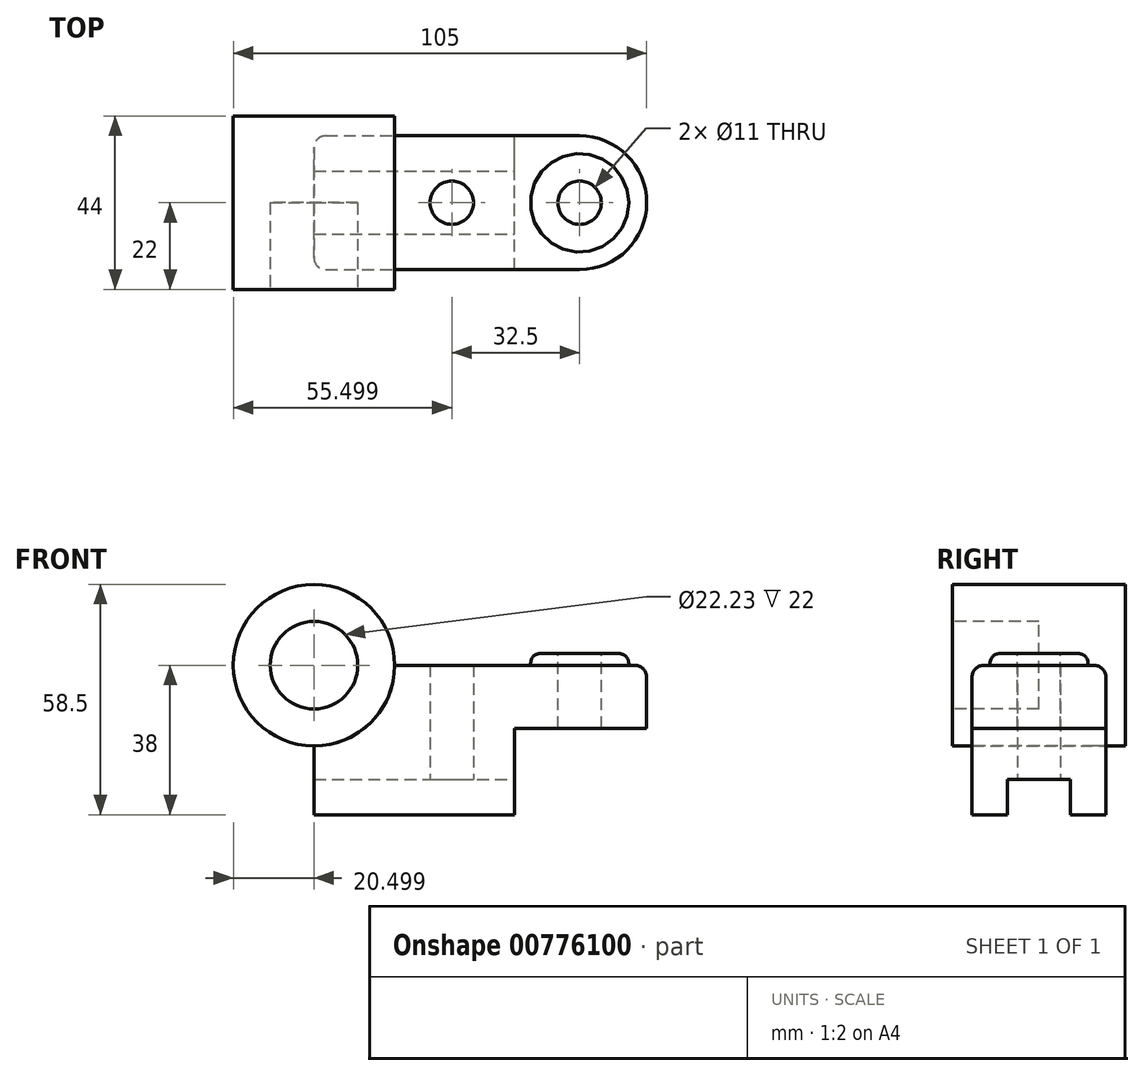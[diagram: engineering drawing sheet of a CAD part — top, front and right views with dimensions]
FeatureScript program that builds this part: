
annotation { "Feature Type Name" : "Feature", "Feature Type Description" : "" }
export const myFeature = defineFeature(function(context is Context, id is Id, definition is map)
    precondition{}
    {
        {
            var Q0;
            Q0=qCreatedBy(makeId("Front.planeOp"),FACE);
            var sketch = newSketch(context, id + "F0", { "sketchPlane" : qUnion([Q0])});
            skLineSegment(sketch, "E0.bottom", {"start": v(-36.23, 1.48) * mm, "end": v(48.27, 1.48) * mm});
            skLineSegment(sketch, "E0.top", {"start": v(-36.23, -36.52) * mm, "end": v(48.27, -36.52) * mm});
            skLineSegment(sketch, "E0.left", {"start": v(-36.23, 1.48) * mm, "end": v(-36.23, -36.52) * mm});
            skLineSegment(sketch, "E0.right", {"start": v(48.27, 1.48) * mm, "end": v(48.27, -36.52) * mm});
            skLineSegment(sketch, "E1", {"start": v(48.27, -36.52) * mm, "end": v(14.77, -36.52) * mm});
            skLineSegment(sketch, "E2", {"start": v(14.77, -36.52) * mm, "end": v(14.77, -14.52) * mm});
            skLineSegment(sketch, "E3", {"start": v(14.77, -14.52) * mm, "end": v(48.27, -14.52) * mm});
            skLineSegment(sketch, "E4", {"start": v(48.27, -14.52) * mm, "end": v(48.27, -36.52) * mm});
            skSolve(sketch);
        }
        {
            var Q0;
            Q0=makeQuery(id+"F0.imprint","IMPRINT",FACE,{"disambiguationData":[TD([[makeQuery(id+"F0.imprint","IMPRINT",EDGE,{"derivedFrom":sQuery(id+"F0.wireOp",EDGE,"E0.bottom")}),-1.0]])]});
            extrude(context, id + "F1", {"entities" : qUnion([Q0]), "depth" : 34 * mm, "offsetDistance" : 25 * mm});
        }
        {
            var Q0;
            Q0=makeQuery(id+"F1.opExtrude","SWEPT_FACE",FACE,{"disambiguationData":[OSD([sQuery(id+"F0.wireOp",EDGE,"E2")])]});
            var sketch = newSketch(context, id + "F2", { "sketchPlane" : qUnion([Q0])});
            skLineSegment(sketch, "E5", {"start": v(-34, -36.52) * mm, "end": v(-25, -36.52) * mm});
            skLineSegment(sketch, "E6", {"start": v(-25, -36.52) * mm, "end": v(-25, -27.52) * mm});
            skLineSegment(sketch, "E7", {"start": v(-25, -27.52) * mm, "end": v(-9, -27.52) * mm});
            skLineSegment(sketch, "E8", {"start": v(-9, -27.52) * mm, "end": v(-9, -36.52) * mm});
            skLineSegment(sketch, "E9", {"start": v(-9, -36.52) * mm, "end": v(-25, -36.52) * mm});
            skSolve(sketch);
        }
        {
            var Q0;
            Q0=makeQuery(id+"F2.imprint","IMPRINT",FACE,{"disambiguationData":[TD([[makeQuery(id+"F2.imprint","IMPRINT",EDGE,{"derivedFrom":sQuery(id+"F2.wireOp",EDGE,"E6")}),-1.0]])]});
            extrude(context, id + "F3", {"entities" : qUnion([Q0]), "operationType" : NewBodyOperationType.REMOVE, "oppositeDirection" : true, "depth" : 100 * mm, "offsetDistance" : 25 * mm});
        }
        {
            var Q0;
            Q0=makeQuery(id+"F1.opExtrude","CAP_EDGE",EDGE,{"disambiguationData":[OSD([sQuery(id+"F0.wireOp",EDGE,"E0.right")])],"isStart":false});
            fillet(context, id + "F4", {"entities" : qUnion([Q0]), "radius" : 17 * mm, "tangentPropagation" : true, "allowEdgeOverflow" : false});
        }
        {
            var Q0;
            Q0=makeQuery(id+"F1.opExtrude","CAP_EDGE",EDGE,{"disambiguationData":[OSD([sQuery(id+"F0.wireOp",EDGE,"E0.right")])],"isStart":true});
            fillet(context, id + "F5", {"entities" : qUnion([Q0]), "radius" : 17 * mm, "tangentPropagation" : true, "allowEdgeOverflow" : false});
        }
        {
            var Q0;
            Q0=makeQuery(id+"F1.opExtrude","SWEPT_FACE",FACE,{"disambiguationData":[OSD([sQuery(id+"F0.wireOp",EDGE,"E0.bottom")])]});
            var sketch = newSketch(context, id + "F6", { "sketchPlane" : qUnion([Q0])});
            skLineSegment(sketch, "E10", {"start": v(31.27, 0) * mm, "end": v(31.27, -17) * mm});
            skCircle(sketch, "E11", {"center": v(31.27, -17) * mm, "radius": 12.5 * mm});
            skCircle(sketch, "E12", {"center": v(31.27, -17) * mm, "radius": 5.5 * mm});
            skSolve(sketch);
        }
        {
            var Q0;
            Q0=makeQuery(id+"F6.imprint","IMPRINT",FACE,{"disambiguationData":[TD([[makeQuery(id+"F6.imprint","IMPRINT",EDGE,{"derivedFrom":sQuery(id+"F6.wireOp",EDGE,"E12")}),1.0]])]});
            extrude(context, id + "F7", {"entities" : qUnion([Q0]), "operationType" : NewBodyOperationType.REMOVE, "oppositeDirection" : true, "depth" : 25 * mm, "offsetDistance" : 25 * mm});
        }
        {
            var Q0;
            Q0=makeQuery(id+"F1.opExtrude","SWEPT_FACE",FACE,{"disambiguationData":[OSD([sQuery(id+"F0.wireOp",EDGE,"E0.bottom")])]});
            var sketch = newSketch(context, id + "F8", { "sketchPlane" : qUnion([Q0])});
            skLineSegment(sketch, "E13", {"start": v(31.27, 0) * mm, "end": v(31.27, -17) * mm});
            skCircle(sketch, "E14", {"center": v(31.27, -17) * mm, "radius": 12.5 * mm});
            skSolve(sketch);
        }
        {
            var Q0;
            Q0=makeQuery(id+"F8.imprint","IMPRINT",FACE,{"disambiguationData":[TD([[makeQuery(id+"F8.imprint","IMPRINT",EDGE,{"derivedFrom":sQuery(id+"F8.wireOp",EDGE,"E14")}),1.0]])]});
            extrude(context, id + "F9", {"entities" : qUnion([Q0]), "operationType" : NewBodyOperationType.ADD, "depth" : 3 * mm, "offsetDistance" : 25 * mm});
        }
        {
            var Q0;
            Q0=makeQuery(id+"F1.opExtrude","CAP_FACE",FACE,{"disambiguationData":[OSD([sQuery(id+"F0.wireOp",EDGE,"E0.bottom"),sQuery(id+"F0.wireOp",EDGE,"E0.top"),sQuery(id+"F0.wireOp",EDGE,"E0.left"),sQuery(id+"F0.wireOp",EDGE,"E0.right"),sQuery(id+"F0.wireOp",EDGE,"E2"),sQuery(id+"F0.wireOp",EDGE,"E3")])],"isStart":false});
            var sketch = newSketch(context, id + "F10", { "sketchPlane" : qUnion([Q0])});
            skCircle(sketch, "E15", {"center": v(-36.23, 1.48) * mm, "radius": 20.5 * mm});
            skCircle(sketch, "E16", {"center": v(-36.23, 1.48) * mm, "radius": 11.12 * mm});
            skSolve(sketch);
        }
        {
            var Q0;
            {var subQ0=sQuery(id+"F10.wireOp",EDGE,"E16");var subQ1=makeQuery(id+"F1.opExtrude","CAP_EDGE",EDGE,{"disambiguationData":[OSD([sQuery(id+"F0.wireOp",EDGE,"E0.left")])],"isStart":false});var subQ2=makeQuery(id+"F10.imprint","INTERSECT",VERTEX,{"derivedFrom":[subQ1,subQ0]});Q0=makeQuery(id+"F10.imprint","IMPRINT",FACE,{"disambiguationData":[TD([[makeQuery(id+"F10.imprint","IMPRINT",EDGE,{"disambiguationData":[TD([[subQ2,-1.0]])],"derivedFrom":subQ0}),1.0]])]});}
            var Q1;
            {var subQ0=sQuery(id+"F10.wireOp",EDGE,"E15");var subQ1=makeQuery(id+"F1.opExtrude","CAP_EDGE",EDGE,{"disambiguationData":[OSD([sQuery(id+"F0.wireOp",EDGE,"E0.left")])],"isStart":false});var subQ2=makeQuery(id+"F10.imprint","INTERSECT",VERTEX,{"derivedFrom":[subQ1,subQ0]});Q1=makeQuery(id+"F10.imprint","IMPRINT",FACE,{"disambiguationData":[TD([[makeQuery(id+"F10.imprint","IMPRINT",EDGE,{"disambiguationData":[TD([[subQ2,-1.0]])],"derivedFrom":subQ0}),1.0]])]});}
            extrude(context, id + "F11", {"entities" : qUnion([Q0, Q1]), "operationType" : NewBodyOperationType.REMOVE, "oppositeDirection" : true, "depth" : 50 * mm, "offsetDistance" : 25 * mm});
        }
        {
            var Q0;
            Q0=qCreatedBy(makeId("Front.planeOp"),FACE);
            var sketch = newSketch(context, id + "F12", { "sketchPlane" : qUnion([Q0])});
            skCircle(sketch, "E17", {"center": v(-36.23, 1.48) * mm, "radius": 20.5 * mm});
            skCircle(sketch, "E18", {"center": v(-36.23, 1.48) * mm, "radius": 11.12 * mm});
            skSolve(sketch);
        }
        {
            var Q0;
            Q0=makeQuery(id+"F12.imprint","IMPRINT",FACE,{"disambiguationData":[TD([[makeQuery(id+"F12.imprint","IMPRINT",EDGE,{"derivedFrom":sQuery(id+"F12.wireOp",EDGE,"E18")}),1.0]])]});
            var Q1;
            Q1=makeQuery(id+"F12.imprint","IMPRINT",FACE,{"disambiguationData":[TD([[makeQuery(id+"F12.imprint","IMPRINT",EDGE,{"derivedFrom":sQuery(id+"F12.wireOp",EDGE,"E17")}),1.0]])]});
            extrude(context, id + "F13", {"entities" : qUnion([Q0, Q1]), "depth" : 5 * mm, "offsetDistance" : 25 * mm});
        }
        {
            var Q0;
            Q0=makeQuery(id+"F13.opExtrude","CAP_FACE",FACE,{"disambiguationData":[OSD([sQuery(id+"F12.wireOp",EDGE,"E17")])],"isStart":false});
            var sketch = newSketch(context, id + "F14", { "sketchPlane" : qUnion([Q0])});
            skCircle(sketch, "E19", {"center": v(-36.23, 1.48) * mm, "radius": 20.5 * mm});
            skSolve(sketch);
        }
        {
            var Q0;
            Q0=qSketchRegion(id+"F14",true);
            extrude(context, id + "F15", {"entities" : qUnion([Q0]), "operationType" : NewBodyOperationType.ADD, "depth" : 39 * mm, "offsetDistance" : 25 * mm});
        }
        {
            var Q0;
            Q0=makeQuery(id+"F13.opExtrude","CAP_FACE",FACE,{"disambiguationData":[OSD([sQuery(id+"F12.wireOp",EDGE,"E17")])],"isStart":true});
            var sketch = newSketch(context, id + "F16", { "sketchPlane" : qUnion([Q0])});
            skCircle(sketch, "E20", {"center": v(36.23, 1.48) * mm, "radius": 20.5 * mm});
            skSolve(sketch);
        }
        {
            var Q0;
            Q0=qSketchRegion(id+"F16",true);
            extrude(context, id + "F17", {"entities" : qUnion([Q0]), "operationType" : NewBodyOperationType.ADD, "depth" : 5 * mm, "offsetDistance" : 25 * mm});
        }
        {
            var Q0;
            Q0=makeQuery(id+"F15.opExtrude","CAP_FACE",FACE,{"disambiguationData":[OSD([sQuery(id+"F14.wireOp",EDGE,"E19")])],"isStart":false});
            var sketch = newSketch(context, id + "F18", { "sketchPlane" : qUnion([Q0])});
            skCircle(sketch, "E21", {"center": v(-36.23, 1.48) * mm, "radius": 20.5 * mm});
            skSolve(sketch);
        }
        {
            var Q0;
            Q0=qSketchRegion(id+"F18",true);
            extrude(context, id + "F19", {"entities" : qUnion([Q0]), "operationType" : NewBodyOperationType.REMOVE, "oppositeDirection" : true, "depth" : 5 * mm, "offsetDistance" : 25 * mm});
        }
        {
            var Q0;
            Q0=makeQuery(id+"F19.boolean.opBoolean","COPY",FACE,{"derivedFrom":makeQuery(id+"F19.opExtrude","CAP_FACE",FACE,{"disambiguationData":[OSD([sQuery(id+"F18.wireOp",EDGE,"E21")])],"isStart":false})});
            var sketch = newSketch(context, id + "F20", { "sketchPlane" : qUnion([Q0])});
            skCircle(sketch, "E22", {"center": v(-36.23, 1.48) * mm, "radius": 11.12 * mm});
            skSolve(sketch);
        }
        {
            var Q0;
            Q0=makeQuery(id+"F20.imprint","IMPRINT",FACE,{"disambiguationData":[TD([[makeQuery(id+"F20.imprint","IMPRINT",EDGE,{"derivedFrom":sQuery(id+"F20.wireOp",EDGE,"E22")}),1.0]])]});
            extrude(context, id + "F21", {"entities" : qUnion([Q0]), "operationType" : NewBodyOperationType.REMOVE, "oppositeDirection" : true, "depth" : 22 * mm, "offsetDistance" : 25 * mm});
        }
        {
            var Q0;
            Q0=makeQuery(id+"F3.boolean.opBoolean","COPY",FACE,{"derivedFrom":makeQuery(id+"F3.opExtrude","SWEPT_FACE",FACE,{"disambiguationData":[OSD([sQuery(id+"F2.wireOp",EDGE,"E7")])]})});
            var sketch = newSketch(context, id + "F22", { "sketchPlane" : qUnion([Q0])});
            skLineSegment(sketch, "E23", {"start": v(-36.23, 9) * mm, "end": v(-36.23, 17) * mm});
            skLineSegment(sketch, "E24", {"start": v(-36.23, 17) * mm, "end": v(-1.23, 17) * mm});
            skCircle(sketch, "E25", {"center": v(-1.23, 17) * mm, "radius": 5.5 * mm});
            skSolve(sketch);
        }
        {
            var Q0;
            Q0=makeQuery(id+"F22.imprint","IMPRINT",FACE,{"disambiguationData":[TD([[makeQuery(id+"F22.imprint","IMPRINT",EDGE,{"derivedFrom":sQuery(id+"F22.wireOp",EDGE,"E25")}),1.0]])]});
            extrude(context, id + "F23", {"entities" : qUnion([Q0]), "operationType" : NewBodyOperationType.REMOVE, "oppositeDirection" : true, "depth" : 25 * mm, "offsetDistance" : 25 * mm});
        }
        {
            var Q0;
            Q0=makeQuery(id+"F23.boolean.opBoolean","COPY",FACE,{"derivedFrom":makeQuery(id+"F23.opExtrude","CAP_FACE",FACE,{"disambiguationData":[OSD([sQuery(id+"F22.wireOp",EDGE,"E25")])],"isStart":false})});
            extrude(context, id + "F24", {"entities" : qUnion([Q0]), "operationType" : NewBodyOperationType.REMOVE, "oppositeDirection" : true, "depth" : 25 * mm, "offsetDistance" : 25 * mm});
        }
        {
            var Q0;
            Q0=makeQuery(id+"F1.opExtrude","CAP_EDGE",EDGE,{"disambiguationData":[OSD([sQuery(id+"F0.wireOp",EDGE,"E0.bottom")])],"isStart":true});
            var Q1;
            Q1=makeQuery(id+"F5.opFillet","BLEND_EDGE",EDGE,{"blendedFrom":[makeQuery(id+"F1.opExtrude","CAP_EDGE",EDGE,{"disambiguationData":[OSD([sQuery(id+"F0.wireOp",EDGE,"E0.right")])],"isStart":true}),makeQuery(id+"F1.opExtrude","SWEPT_FACE",FACE,{"disambiguationData":[OSD([sQuery(id+"F0.wireOp",EDGE,"E0.bottom")])]})],"blendedInto":[makeQuery(id+"F1.opExtrude","SWEPT_FACE",FACE,{"disambiguationData":[OSD([sQuery(id+"F0.wireOp",EDGE,"E0.bottom")])]})]});
            var Q2;
            Q2=makeQuery(id+"F4.opFillet","BLEND_EDGE",EDGE,{"blendedFrom":[makeQuery(id+"F1.opExtrude","CAP_EDGE",EDGE,{"disambiguationData":[OSD([sQuery(id+"F0.wireOp",EDGE,"E0.right")])],"isStart":false}),makeQuery(id+"F1.opExtrude","SWEPT_FACE",FACE,{"disambiguationData":[OSD([sQuery(id+"F0.wireOp",EDGE,"E0.bottom")])]})],"blendedInto":[makeQuery(id+"F1.opExtrude","SWEPT_FACE",FACE,{"disambiguationData":[OSD([sQuery(id+"F0.wireOp",EDGE,"E0.bottom")])]})]});
            var Q3;
            Q3=makeQuery(id+"F1.opExtrude","CAP_EDGE",EDGE,{"disambiguationData":[OSD([sQuery(id+"F0.wireOp",EDGE,"E0.bottom")])],"isStart":false});
            var Q4;
            Q4=makeQuery(id+"F11.boolean.opBoolean","COPY",EDGE,{"derivedFrom":makeQuery(id+"F11.opExtrude","SWEPT_EDGE",EDGE,{"disambiguationData":[OSD([sQuery(id+"F0.wireOp",EDGE,"E0.bottom"),sQuery(id+"F10.wireOp",EDGE,"E15")])]})});
            fillet(context, id + "F25", {"entities" : qUnion([Q0, Q1, Q2, Q3, Q4]), "radius" : 3.1 * mm, "tangentPropagation" : true, "allowEdgeOverflow" : false});
        }
        {
            var Q0;
            Q0=makeQuery(id+"F1.opExtrude","CAP_EDGE",EDGE,{"disambiguationData":[OSD([sQuery(id+"F0.wireOp",EDGE,"E0.left")])],"isStart":true});
            var Q1;
            Q1=makeQuery(id+"F1.opExtrude","CAP_EDGE",EDGE,{"disambiguationData":[OSD([sQuery(id+"F0.wireOp",EDGE,"E0.left")])],"isStart":false});
            fillet(context, id + "F26", {"entities" : qUnion([Q0, Q1]), "radius" : 3 * mm, "tangentPropagation" : true, "allowEdgeOverflow" : false});
        }
        {
            var Q0;
            Q0=makeQuery(id+"F9.opExtrude","CAP_EDGE",EDGE,{"disambiguationData":[OSD([sQuery(id+"F8.wireOp",EDGE,"E14")])],"isStart":false});
            fillet(context, id + "F27", {"entities" : qUnion([Q0]), "radius" : 3 * mm, "rho" : 0.5, "crossSection" : FilletCrossSection.CONIC, "allowEdgeOverflow" : false});
        }
    });
